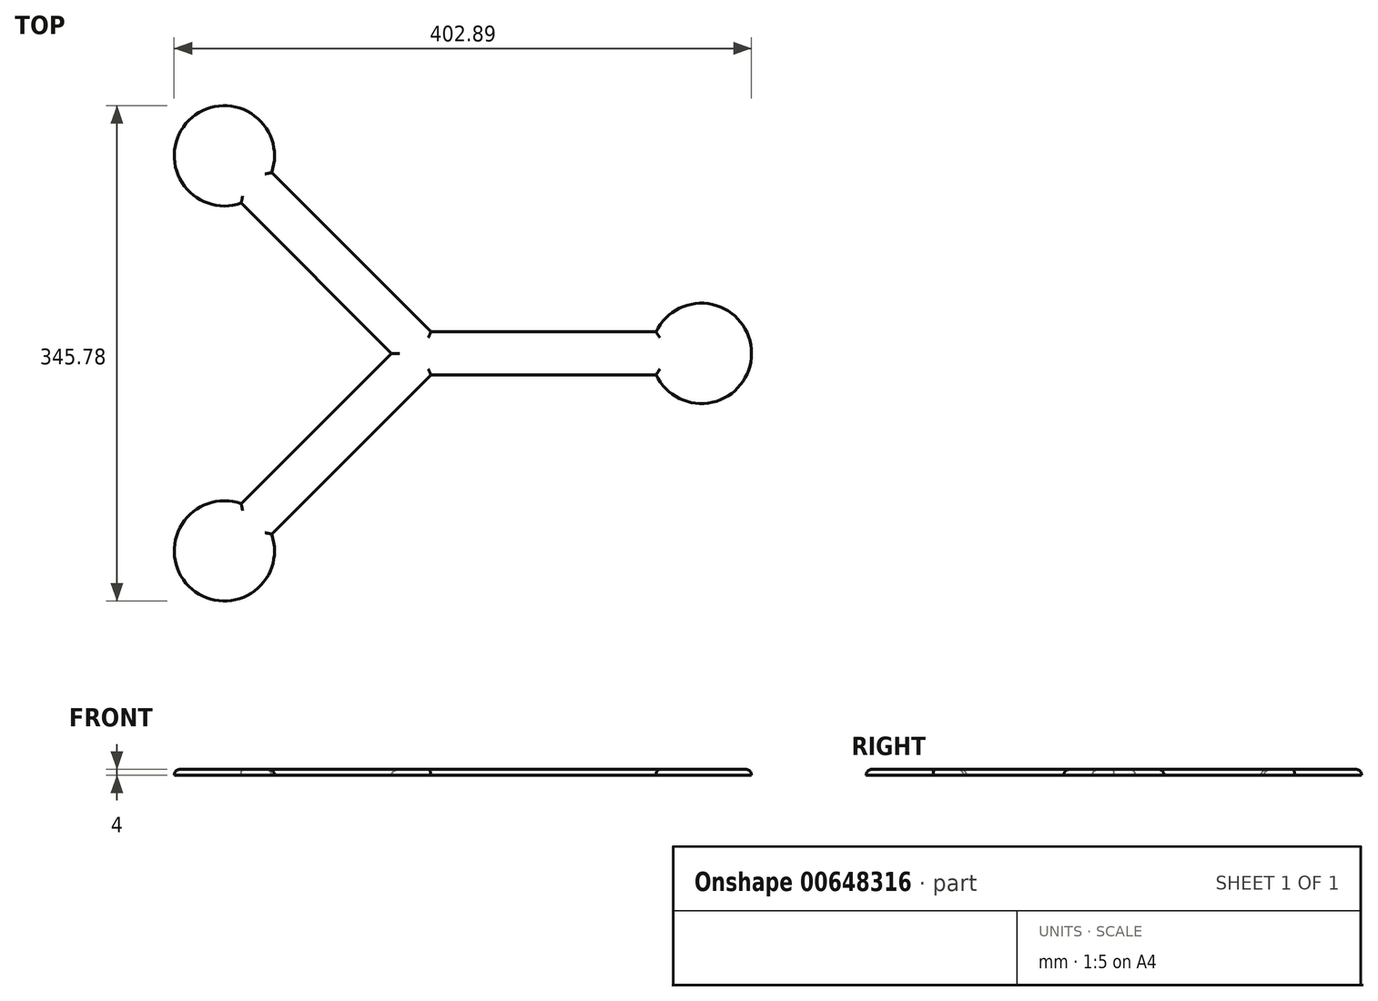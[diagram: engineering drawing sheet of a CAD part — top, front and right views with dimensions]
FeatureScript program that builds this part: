
annotation { "Feature Type Name" : "Feature", "Feature Type Description" : "" }
export const myFeature = defineFeature(function(context is Context, id is Id, definition is map)
    precondition{}
    {
        {
            var Q0;
            Q0=qCreatedBy(makeId("Top.planeOp"),FACE);
            var sketch = newSketch(context, id + "F0", { "sketchPlane" : qUnion([Q0])});
            skArc(sketch, "E0", {"start": v(163.38, -15) * mm, "mid": v(230, 0) * mm, "end": v(163.38, 15) * mm});
            skArc(sketch, "E1", {"start": v(-104.92, 126.13) * mm, "mid": v(-162.63, 162.63) * mm, "end": v(-126.13, 104.92) * mm});
            skArc(sketch, "E2", {"start": v(-126.13, -104.92) * mm, "mid": v(-162.63, -162.63) * mm, "end": v(-104.92, -126.13) * mm});
            skLineSegment(sketch, "E3.0", {"start": v(6.21, -15) * mm, "end": v(163.38, -15) * mm});
            skLineSegment(sketch, "E3.1", {"start": v(6.21, -15) * mm, "end": v(-104.92, -126.13) * mm});
            skLineSegment(sketch, "E4.0", {"start": v(6.21, 15) * mm, "end": v(163.38, 15) * mm});
            skLineSegment(sketch, "E4.1", {"start": v(6.21, 15) * mm, "end": v(-104.92, 126.13) * mm});
            skLineSegment(sketch, "E5.0", {"start": v(-21.21, 0) * mm, "end": v(-126.13, 104.92) * mm});
            skLineSegment(sketch, "E5.1", {"start": v(-21.21, 0) * mm, "end": v(-126.13, -104.92) * mm});
            skSolve(sketch);
        }
        {
            var Q0;
            Q0 = qSketchRegion(id + "F0", true);
            extrude(context, id + "F1", {"entities" : qUnion([Q0]), "depth" : 4 * mm, "offsetDistance" : 25 * mm});
        }
        {
            var Q0;
            Q0=makeQuery(id+"F1.opExtrude","CAP_FACE",FACE,{"disambiguationData":[OSD([sQuery(id+"F0.wireOp",EDGE,"E0"),sQuery(id+"F0.wireOp",EDGE,"E1"),sQuery(id+"F0.wireOp",EDGE,"E2"),sQuery(id+"F0.wireOp",EDGE,"E3.0"),sQuery(id+"F0.wireOp",EDGE,"E3.1"),sQuery(id+"F0.wireOp",EDGE,"E4.0"),sQuery(id+"F0.wireOp",EDGE,"E4.1"),sQuery(id+"F0.wireOp",EDGE,"E5.0"),sQuery(id+"F0.wireOp",EDGE,"E5.1")])],"isStart":false});
            fillet(context, id + "F2", {"entities" : qUnion([Q0]), "radius" : 4 * mm, "tangentPropagation" : true, "allowEdgeOverflow" : false});
        }
    });
